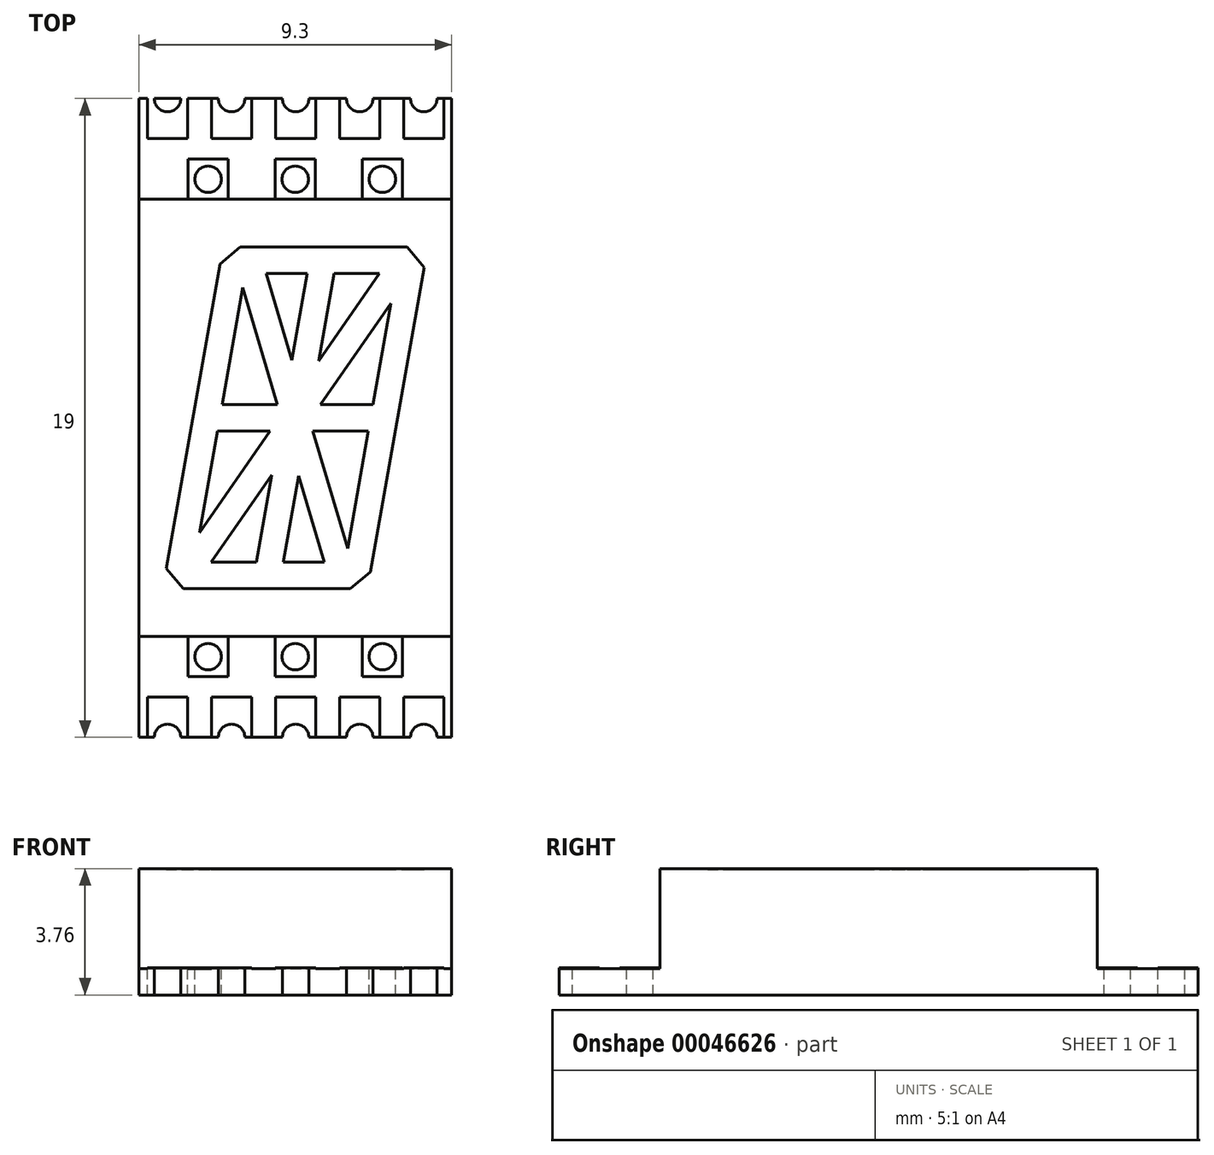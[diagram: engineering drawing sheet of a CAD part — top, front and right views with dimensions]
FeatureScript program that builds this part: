
annotation { "Feature Type Name" : "Feature", "Feature Type Description" : "" }
export const myFeature = defineFeature(function(context is Context, id is Id, definition is map)
    precondition{}
    {
        {
            var Q0;
            Q0=qCreatedBy(makeId("Top.planeOp"),FACE);
            var sketch = newSketch(context, id + "F0", { "sketchPlane" : qUnion([Q0])});
            skLineSegment(sketch, "E0.bottom", {"start": v(-4.65, -9.5) * mm, "end": v(4.65, -9.5) * mm});
            skLineSegment(sketch, "E0.top", {"start": v(-4.65, 9.5) * mm, "end": v(4.65, 9.5) * mm});
            skLineSegment(sketch, "E0.left", {"start": v(-4.65, -9.5) * mm, "end": v(-4.65, 9.5) * mm});
            skLineSegment(sketch, "E0.right", {"start": v(4.65, -9.5) * mm, "end": v(4.65, 9.5) * mm});
            skSolve(sketch);
        }
        {
            var Q0;
            Q0=makeQuery(id+"F0.imprint","IMPRINT",FACE,{"disambiguationData":[TD([[makeQuery(id+"F0.imprint","IMPRINT",EDGE,{"derivedFrom":sQuery(id+"F0.wireOp",EDGE,"E0.bottom")}),1.0]])]});
            extrude(context, id + "F1", {"entities" : qUnion([Q0]), "depth" : 0.79 * mm});
        }
        {
            var Q0;
            Q0=makeQuery(id+"F1.opExtrude","CAP_FACE",FACE,{"disambiguationData":[OSD([sQuery(id+"F0.wireOp",EDGE,"E0.bottom"),sQuery(id+"F0.wireOp",EDGE,"E0.top"),sQuery(id+"F0.wireOp",EDGE,"E0.left"),sQuery(id+"F0.wireOp",EDGE,"E0.right")])],"isStart":false});
            var sketch = newSketch(context, id + "F2", { "sketchPlane" : qUnion([Q0])});
            skLineSegment(sketch, "E1.bottom", {"start": v(-4.65, -6.5) * mm, "end": v(4.65, -6.5) * mm});
            skLineSegment(sketch, "E1.top", {"start": v(-4.65, 6.5) * mm, "end": v(4.65, 6.5) * mm});
            skLineSegment(sketch, "E1.left", {"start": v(-4.65, -6.5) * mm, "end": v(-4.65, 6.5) * mm});
            skLineSegment(sketch, "E1.right", {"start": v(4.65, -6.5) * mm, "end": v(4.65, 6.5) * mm});
            skSolve(sketch);
        }
        {
            var Q0;
            Q0=makeQuery(id+"F2.imprint","IMPRINT",FACE,{"disambiguationData":[TD([[makeQuery(id+"F2.imprint","IMPRINT",EDGE,{"derivedFrom":sQuery(id+"F2.wireOp",EDGE,"E1.bottom")}),1.0]])]});
            extrude(context, id + "F3", {"entities" : qUnion([Q0]), "operationType" : NewBodyOperationType.ADD, "depth" : 2.97 * mm});
        }
        {
            var Q0;
            {var subQ0=sQuery(id+"F0.wireOp",EDGE,"E0.bottom");var subQ1=sQuery(id+"F0.wireOp",EDGE,"E0.left");var subQ2=sQuery(id+"F0.wireOp",EDGE,"E0.right");Q0=makeQuery(id+"F3.boolean.opBoolean","SPLIT",FACE,{"disambiguationData":[TD([makeQuery(id+"F1.opExtrude","SWEPT_FACE",FACE,{"disambiguationData":[OSD([subQ0])]})])],"derivedFrom":makeQuery(id+"F1.opExtrude","CAP_FACE",FACE,{"disambiguationData":[OSD([subQ0,sQuery(id+"F0.wireOp",EDGE,"E0.top"),subQ1,subQ2])],"isStart":false})});}
            var sketch = newSketch(context, id + "F4", { "sketchPlane" : qUnion([Q0])});
            skLineSegment(sketch, "E2", {"start": v(-4.4, -9.5) * mm, "end": v(-4.4, -8.3) * mm});
            skLineSegment(sketch, "E3", {"start": v(-4.4, -8.3) * mm, "end": v(-3.2, -8.3) * mm});
            skLineSegment(sketch, "E4", {"start": v(-3.2, -8.3) * mm, "end": v(-3.2, -9.5) * mm});
            skArc(sketch, "E5", {"start": v(-3.4, -9.5) * mm, "mid": v(-3.8, -9.1) * mm, "end": v(-4.2, -9.5) * mm});
            skLineSegment(sketch, "E6", {"start": v(-4.4, -9.5) * mm, "end": v(-4.2, -9.5) * mm});
            skLineSegment(sketch, "E7", {"start": v(-3.4, -9.5) * mm, "end": v(-3.2, -9.5) * mm});
            skLineSegment(sketch, "E8", {"start": v(-4.2, -9.5) * mm, "end": v(-3.4, -9.5) * mm});
            skLineSegment(sketch, "E9.1.0.0", {"start": v(-2.49, -8.3) * mm, "end": v(-1.3, -8.3) * mm});
            skLineSegment(sketch, "E9.1.0.1", {"start": v(-2.49, -9.5) * mm, "end": v(-2.49, -8.3) * mm});
            skLineSegment(sketch, "E9.1.0.2", {"start": v(-1.3, -8.3) * mm, "end": v(-1.3, -9.5) * mm});
            skArc(sketch, "E9.1.0.3", {"start": v(-1.5, -9.5) * mm, "mid": v(-1.9, -9.1) * mm, "end": v(-2.29, -9.5) * mm});
            skLineSegment(sketch, "E9.1.0.4", {"start": v(-2.29, -9.5) * mm, "end": v(-1.5, -9.5) * mm});
            skLineSegment(sketch, "E9.1.0.5", {"start": v(-2.49, -9.5) * mm, "end": v(-2.29, -9.5) * mm});
            skLineSegment(sketch, "E9.1.0.6", {"start": v(-1.5, -9.5) * mm, "end": v(-1.3, -9.5) * mm});
            skLineSegment(sketch, "E9.2.0.0", {"start": v(-0.58, -8.3) * mm, "end": v(0.6, -8.3) * mm});
            skLineSegment(sketch, "E9.2.0.1", {"start": v(-0.58, -9.5) * mm, "end": v(-0.58, -8.3) * mm});
            skLineSegment(sketch, "E9.2.0.2", {"start": v(0.6, -8.3) * mm, "end": v(0.6, -9.5) * mm});
            skArc(sketch, "E9.2.0.3", {"start": v(0.4, -9.5) * mm, "mid": v(0.01, -9.1) * mm, "end": v(-0.38, -9.5) * mm});
            skLineSegment(sketch, "E9.2.0.4", {"start": v(-0.38, -9.5) * mm, "end": v(0.4, -9.5) * mm});
            skLineSegment(sketch, "E9.2.0.5", {"start": v(-0.58, -9.5) * mm, "end": v(-0.38, -9.5) * mm});
            skLineSegment(sketch, "E9.2.0.6", {"start": v(0.4, -9.5) * mm, "end": v(0.6, -9.5) * mm});
            skLineSegment(sketch, "E9.3.0.0", {"start": v(1.32, -8.3) * mm, "end": v(2.51, -8.3) * mm});
            skLineSegment(sketch, "E9.3.0.1", {"start": v(1.32, -9.5) * mm, "end": v(1.32, -8.3) * mm});
            skLineSegment(sketch, "E9.3.0.2", {"start": v(2.51, -8.3) * mm, "end": v(2.51, -9.5) * mm});
            skArc(sketch, "E9.3.0.3", {"start": v(2.31, -9.5) * mm, "mid": v(1.92, -9.1) * mm, "end": v(1.52, -9.5) * mm});
            skLineSegment(sketch, "E9.3.0.4", {"start": v(1.52, -9.5) * mm, "end": v(2.31, -9.5) * mm});
            skLineSegment(sketch, "E9.3.0.5", {"start": v(1.32, -9.5) * mm, "end": v(1.52, -9.5) * mm});
            skLineSegment(sketch, "E9.3.0.6", {"start": v(2.31, -9.5) * mm, "end": v(2.51, -9.5) * mm});
            skLineSegment(sketch, "E9.4.0.0", {"start": v(3.23, -8.3) * mm, "end": v(4.42, -8.3) * mm});
            skLineSegment(sketch, "E9.4.0.1", {"start": v(3.23, -9.5) * mm, "end": v(3.23, -8.3) * mm});
            skLineSegment(sketch, "E9.4.0.2", {"start": v(4.42, -8.3) * mm, "end": v(4.42, -9.5) * mm});
            skArc(sketch, "E9.4.0.3", {"start": v(4.22, -9.5) * mm, "mid": v(3.82, -9.1) * mm, "end": v(3.43, -9.5) * mm});
            skLineSegment(sketch, "E9.4.0.4", {"start": v(3.43, -9.5) * mm, "end": v(4.22, -9.5) * mm});
            skLineSegment(sketch, "E9.4.0.5", {"start": v(3.23, -9.5) * mm, "end": v(3.43, -9.5) * mm});
            skLineSegment(sketch, "E9.4.0.6", {"start": v(4.22, -9.5) * mm, "end": v(4.42, -9.5) * mm});
            skLineSegment(sketch, "E9.direction1", {"start": v(-4.4, -8.3) * mm, "end": v(-2.49, -8.3) * mm, "construction": true});
            skLineSegment(sketch, "E10", {"start": v(-9.42, 0) * mm, "end": v(7.06, 0) * mm, "construction": true});
            skLineSegment(sketch, "E11.MirrorCS", {"start": v(-1.5, 9.5) * mm, "end": v(-1.3, 9.5) * mm});
            skLineSegment(sketch, "E12.MirrorCS", {"start": v(-2.49, 9.5) * mm, "end": v(-2.29, 9.5) * mm});
            skLineSegment(sketch, "E13.MirrorCS", {"start": v(-2.29, 9.5) * mm, "end": v(-1.5, 9.5) * mm});
            skArc(sketch, "E14.MirrorCS", {"start": v(-1.5, 9.5) * mm, "mid": v(-1.9, 9.1) * mm, "end": v(-2.29, 9.5) * mm});
            skLineSegment(sketch, "E15.MirrorCS", {"start": v(-0.58, 9.5) * mm, "end": v(-0.38, 9.5) * mm});
            skArc(sketch, "E16.MirrorCS", {"start": v(-3.4, 9.5) * mm, "mid": v(-3.8, 9.1) * mm, "end": v(-4.2, 9.5) * mm});
            skLineSegment(sketch, "E17.MirrorCS", {"start": v(-3.4, 9.5) * mm, "end": v(-3.2, 9.5) * mm});
            skLineSegment(sketch, "E18.MirrorCS", {"start": v(-4.2, 9.5) * mm, "end": v(-3.4, 9.5) * mm});
            skLineSegment(sketch, "E19.MirrorCS", {"start": v(-0.38, 9.5) * mm, "end": v(0.4, 9.5) * mm});
            skLineSegment(sketch, "E20.MirrorCS", {"start": v(1.32, 9.5) * mm, "end": v(1.52, 9.5) * mm});
            skLineSegment(sketch, "E21.MirrorCS", {"start": v(1.52, 9.5) * mm, "end": v(2.31, 9.5) * mm});
            skArc(sketch, "E22.MirrorCS", {"start": v(0.4, 9.5) * mm, "mid": v(0.01, 9.1) * mm, "end": v(-0.38, 9.5) * mm});
            skLineSegment(sketch, "E23.MirrorCS", {"start": v(3.23, 9.5) * mm, "end": v(3.43, 9.5) * mm});
            skLineSegment(sketch, "E24.MirrorCS", {"start": v(2.31, 9.5) * mm, "end": v(2.51, 9.5) * mm});
            skLineSegment(sketch, "E25.MirrorCS", {"start": v(0.4, 9.5) * mm, "end": v(0.6, 9.5) * mm});
            skArc(sketch, "E26.MirrorCS", {"start": v(2.31, 9.5) * mm, "mid": v(1.92, 9.1) * mm, "end": v(1.52, 9.5) * mm});
            skLineSegment(sketch, "E27.MirrorCS", {"start": v(-4.4, 9.5) * mm, "end": v(-4.2, 9.5) * mm});
            skLineSegment(sketch, "E28.MirrorCS", {"start": v(4.22, 9.5) * mm, "end": v(4.42, 9.5) * mm});
            skLineSegment(sketch, "E29.MirrorCS", {"start": v(3.43, 9.5) * mm, "end": v(4.22, 9.5) * mm});
            skArc(sketch, "E30.MirrorCS", {"start": v(4.22, 9.5) * mm, "mid": v(3.82, 9.1) * mm, "end": v(3.43, 9.5) * mm});
            skLineSegment(sketch, "E31.MirrorCS", {"start": v(-4.4, 8.3) * mm, "end": v(-2.49, 8.3) * mm});
            skLineSegment(sketch, "E32.MirrorCS", {"start": v(-2.49, 9.5) * mm, "end": v(-2.49, 8.3) * mm});
            skLineSegment(sketch, "E33.MirrorCS", {"start": v(-1.3, 8.3) * mm, "end": v(-1.3, 9.5) * mm});
            skLineSegment(sketch, "E34.MirrorCS", {"start": v(-3.2, 8.3) * mm, "end": v(-3.2, 9.5) * mm});
            skLineSegment(sketch, "E35.MirrorCS", {"start": v(-4.4, 8.3) * mm, "end": v(-3.2, 8.3) * mm});
            skLineSegment(sketch, "E36.MirrorCS", {"start": v(-4.4, 9.5) * mm, "end": v(-4.4, 8.3) * mm});
            skLineSegment(sketch, "E37.MirrorCS", {"start": v(2.51, 8.3) * mm, "end": v(2.51, 9.5) * mm});
            skLineSegment(sketch, "E38.MirrorCS", {"start": v(1.32, 9.5) * mm, "end": v(1.32, 8.3) * mm});
            skLineSegment(sketch, "E39.MirrorCS", {"start": v(1.32, 8.3) * mm, "end": v(2.51, 8.3) * mm});
            skLineSegment(sketch, "E40.MirrorCS", {"start": v(4.42, 8.3) * mm, "end": v(4.42, 9.5) * mm});
            skLineSegment(sketch, "E41.MirrorCS", {"start": v(-2.49, 8.3) * mm, "end": v(-1.3, 8.3) * mm});
            skLineSegment(sketch, "E42.MirrorCS", {"start": v(0.6, 8.3) * mm, "end": v(0.6, 9.5) * mm});
            skLineSegment(sketch, "E43.MirrorCS", {"start": v(3.23, 9.5) * mm, "end": v(3.23, 8.3) * mm});
            skLineSegment(sketch, "E44.MirrorCS", {"start": v(3.23, 8.3) * mm, "end": v(4.42, 8.3) * mm});
            skLineSegment(sketch, "E45.MirrorCS", {"start": v(-0.58, 8.3) * mm, "end": v(0.6, 8.3) * mm});
            skLineSegment(sketch, "E46.MirrorCS", {"start": v(-0.58, 9.5) * mm, "end": v(-0.58, 8.3) * mm});
            skLineSegment(sketch, "E47.bottom", {"start": v(-3.19, -6.5) * mm, "end": v(-2, -6.5) * mm});
            skLineSegment(sketch, "E47.top", {"start": v(-3.19, -7.7) * mm, "end": v(-2, -7.7) * mm});
            skLineSegment(sketch, "E47.left", {"start": v(-3.19, -6.5) * mm, "end": v(-3.19, -7.7) * mm});
            skLineSegment(sketch, "E47.right", {"start": v(-2, -6.5) * mm, "end": v(-2, -7.7) * mm});
            skCircle(sketch, "E48", {"center": v(-2.6, -7.1) * mm, "radius": 0.4 * mm});
            skLineSegment(sketch, "E49", {"start": v(-3.19, -6.5) * mm, "end": v(-2, -7.7) * mm, "construction": true});
            skLineSegment(sketch, "E50.1.0.0", {"start": v(-0.6, -6.5) * mm, "end": v(-0.6, -7.7) * mm});
            skLineSegment(sketch, "E50.1.0.1", {"start": v(-0.6, -6.5) * mm, "end": v(0.6, -7.7) * mm, "construction": true});
            skLineSegment(sketch, "E50.1.0.2", {"start": v(-0.6, -6.5) * mm, "end": v(0.6, -6.5) * mm});
            skLineSegment(sketch, "E50.1.0.3", {"start": v(-0.6, -7.7) * mm, "end": v(0.6, -7.7) * mm});
            skCircle(sketch, "E50.1.0.4", {"center": v(0, -7.1) * mm, "radius": 0.4 * mm});
            skLineSegment(sketch, "E50.1.0.5", {"start": v(0.6, -6.5) * mm, "end": v(0.6, -7.7) * mm});
            skLineSegment(sketch, "E50.2.0.0", {"start": v(2, -6.5) * mm, "end": v(2, -7.7) * mm});
            skLineSegment(sketch, "E50.2.0.1", {"start": v(2, -6.5) * mm, "end": v(3.19, -7.7) * mm, "construction": true});
            skLineSegment(sketch, "E50.2.0.2", {"start": v(2, -6.5) * mm, "end": v(3.19, -6.5) * mm});
            skLineSegment(sketch, "E50.2.0.3", {"start": v(2, -7.7) * mm, "end": v(3.19, -7.7) * mm});
            skCircle(sketch, "E50.2.0.4", {"center": v(2.6, -7.1) * mm, "radius": 0.4 * mm});
            skLineSegment(sketch, "E50.2.0.5", {"start": v(3.19, -6.5) * mm, "end": v(3.19, -7.7) * mm});
            skLineSegment(sketch, "E50.direction1", {"start": v(-3.19, -7.7) * mm, "end": v(-0.6, -7.7) * mm, "construction": true});
            skLineSegment(sketch, "E51.MirrorCS", {"start": v(-3.19, 6.5) * mm, "end": v(-2, 7.7) * mm});
            skLineSegment(sketch, "E52.MirrorCS", {"start": v(2, 6.5) * mm, "end": v(3.19, 7.7) * mm});
            skLineSegment(sketch, "E53.MirrorCS", {"start": v(-0.6, 6.5) * mm, "end": v(-0.6, 7.7) * mm});
            skLineSegment(sketch, "E54.MirrorCS", {"start": v(-0.6, 6.5) * mm, "end": v(0.6, 7.7) * mm});
            skLineSegment(sketch, "E55.MirrorCS", {"start": v(-3.19, 6.5) * mm, "end": v(-3.19, 7.7) * mm});
            skLineSegment(sketch, "E56.MirrorCS", {"start": v(-2, 6.5) * mm, "end": v(-2, 7.7) * mm});
            skCircle(sketch, "E57.MirrorC", {"center": v(0, 7.1) * mm, "radius": 0.4 * mm});
            skLineSegment(sketch, "E58.MirrorCS", {"start": v(-3.19, 6.5) * mm, "end": v(-2, 6.5) * mm});
            skLineSegment(sketch, "E59.MirrorCS", {"start": v(-0.6, 6.5) * mm, "end": v(0.6, 6.5) * mm});
            skLineSegment(sketch, "E60.MirrorCS", {"start": v(2, 6.5) * mm, "end": v(2, 7.7) * mm});
            skLineSegment(sketch, "E61.MirrorCS", {"start": v(2, 6.5) * mm, "end": v(3.19, 6.5) * mm});
            skLineSegment(sketch, "E62.MirrorCS", {"start": v(2, 7.7) * mm, "end": v(3.19, 7.7) * mm});
            skCircle(sketch, "E63.MirrorC", {"center": v(2.6, 7.1) * mm, "radius": 0.4 * mm});
            skLineSegment(sketch, "E64.MirrorCS", {"start": v(-3.19, 7.7) * mm, "end": v(-0.6, 7.7) * mm});
            skLineSegment(sketch, "E65.MirrorCS", {"start": v(-0.6, 7.7) * mm, "end": v(0.6, 7.7) * mm});
            skLineSegment(sketch, "E66.MirrorCS", {"start": v(0.6, 6.5) * mm, "end": v(0.6, 7.7) * mm});
            skCircle(sketch, "E67.MirrorC", {"center": v(-2.6, 7.1) * mm, "radius": 0.4 * mm});
            skLineSegment(sketch, "E68.MirrorCS", {"start": v(-3.19, 7.7) * mm, "end": v(-2, 7.7) * mm});
            skLineSegment(sketch, "E69.MirrorCS", {"start": v(3.19, 6.5) * mm, "end": v(3.19, 7.7) * mm});
            skSolve(sketch);
        }
        {
            var Q0;
            Q0=makeQuery(id+"F4.imprint","IMPRINT",FACE,{"disambiguationData":[TD([[makeQuery(id+"F4.imprint","IMPRINT",EDGE,{"derivedFrom":sQuery(id+"F4.wireOp",EDGE,"E5")}),1.0]])]});
            var Q1;
            Q1=makeQuery(id+"F4.imprint","IMPRINT",FACE,{"disambiguationData":[TD([[makeQuery(id+"F4.imprint","IMPRINT",EDGE,{"derivedFrom":sQuery(id+"F4.wireOp",EDGE,"E9.1.0.3")}),1.0]])]});
            var Q2;
            Q2=makeQuery(id+"F4.imprint","IMPRINT",FACE,{"disambiguationData":[TD([[makeQuery(id+"F4.imprint","IMPRINT",EDGE,{"derivedFrom":sQuery(id+"F4.wireOp",EDGE,"E9.2.0.3")}),1.0]])]});
            var Q3;
            Q3=makeQuery(id+"F4.imprint","IMPRINT",FACE,{"disambiguationData":[TD([[makeQuery(id+"F4.imprint","IMPRINT",EDGE,{"derivedFrom":sQuery(id+"F4.wireOp",EDGE,"E9.3.0.3")}),1.0]])]});
            var Q4;
            Q4=makeQuery(id+"F4.imprint","IMPRINT",FACE,{"disambiguationData":[TD([[makeQuery(id+"F4.imprint","IMPRINT",EDGE,{"derivedFrom":sQuery(id+"F4.wireOp",EDGE,"E9.4.0.3")}),1.0]])]});
            var Q5;
            Q5=makeQuery(id+"F4.imprint","IMPRINT",FACE,{"disambiguationData":[TD([[makeQuery(id+"F4.imprint","IMPRINT",EDGE,{"derivedFrom":sQuery(id+"F4.wireOp",EDGE,"E50.2.0.4")}),1.0]])]});
            var Q6;
            Q6=makeQuery(id+"F4.imprint","IMPRINT",FACE,{"disambiguationData":[TD([[makeQuery(id+"F4.imprint","IMPRINT",EDGE,{"derivedFrom":sQuery(id+"F4.wireOp",EDGE,"E50.1.0.4")}),1.0]])]});
            var Q7;
            Q7=makeQuery(id+"F4.imprint","IMPRINT",FACE,{"disambiguationData":[TD([[makeQuery(id+"F4.imprint","IMPRINT",EDGE,{"derivedFrom":sQuery(id+"F4.wireOp",EDGE,"E48")}),1.0]])]});
            var Q8;
            {var subQ0=sQuery(id+"F4.wireOp",EDGE,"E67.MirrorC");var subQ1=sQuery(id+"F4.wireOp",EDGE,"E51.MirrorCS");var subQ3=makeQuery(id+"F4.imprint","INTERSECT",VERTEX,{"disambiguationData":[OD(0.0)],"derivedFrom":[subQ1,subQ0]});Q8=makeQuery(id+"F4.imprint","IMPRINT",FACE,{"disambiguationData":[TD([[makeQuery(id+"F4.imprint","IMPRINT",EDGE,{"disambiguationData":[TD([[subQ3,-1.0]])],"derivedFrom":subQ1}),1.0]])]});}
            var Q9;
            {var subQ0=sQuery(id+"F4.wireOp",EDGE,"E67.MirrorC");var subQ1=sQuery(id+"F4.wireOp",EDGE,"E51.MirrorCS");var subQ3=makeQuery(id+"F4.imprint","INTERSECT",VERTEX,{"disambiguationData":[OD(0.0)],"derivedFrom":[subQ1,subQ0]});Q9=makeQuery(id+"F4.imprint","IMPRINT",FACE,{"disambiguationData":[TD([[makeQuery(id+"F4.imprint","IMPRINT",EDGE,{"disambiguationData":[TD([[subQ3,-1.0]])],"derivedFrom":subQ1}),-1.0]])]});}
            var Q10;
            {var subQ0=sQuery(id+"F4.wireOp",EDGE,"E57.MirrorC");var subQ1=sQuery(id+"F4.wireOp",EDGE,"E54.MirrorCS");var subQ3=makeQuery(id+"F4.imprint","INTERSECT",VERTEX,{"disambiguationData":[OD(0.0)],"derivedFrom":[subQ1,subQ0]});Q10=makeQuery(id+"F4.imprint","IMPRINT",FACE,{"disambiguationData":[TD([[makeQuery(id+"F4.imprint","IMPRINT",EDGE,{"disambiguationData":[TD([[subQ3,-1.0]])],"derivedFrom":subQ1}),1.0]])]});}
            var Q11;
            {var subQ0=sQuery(id+"F4.wireOp",EDGE,"E57.MirrorC");var subQ1=sQuery(id+"F4.wireOp",EDGE,"E54.MirrorCS");var subQ3=makeQuery(id+"F4.imprint","INTERSECT",VERTEX,{"disambiguationData":[OD(0.0)],"derivedFrom":[subQ1,subQ0]});Q11=makeQuery(id+"F4.imprint","IMPRINT",FACE,{"disambiguationData":[TD([[makeQuery(id+"F4.imprint","IMPRINT",EDGE,{"disambiguationData":[TD([[subQ3,-1.0]])],"derivedFrom":subQ1}),-1.0]])]});}
            var Q12;
            {var subQ0=sQuery(id+"F4.wireOp",EDGE,"E63.MirrorC");var subQ1=sQuery(id+"F4.wireOp",EDGE,"E52.MirrorCS");var subQ3=makeQuery(id+"F4.imprint","INTERSECT",VERTEX,{"disambiguationData":[OD(0.0)],"derivedFrom":[subQ1,subQ0]});Q12=makeQuery(id+"F4.imprint","IMPRINT",FACE,{"disambiguationData":[TD([[makeQuery(id+"F4.imprint","IMPRINT",EDGE,{"disambiguationData":[TD([[subQ3,-1.0]])],"derivedFrom":subQ1}),1.0]])]});}
            var Q13;
            {var subQ0=sQuery(id+"F4.wireOp",EDGE,"E63.MirrorC");var subQ1=sQuery(id+"F4.wireOp",EDGE,"E52.MirrorCS");var subQ3=makeQuery(id+"F4.imprint","INTERSECT",VERTEX,{"disambiguationData":[OD(0.0)],"derivedFrom":[subQ1,subQ0]});Q13=makeQuery(id+"F4.imprint","IMPRINT",FACE,{"disambiguationData":[TD([[makeQuery(id+"F4.imprint","IMPRINT",EDGE,{"disambiguationData":[TD([[subQ3,-1.0]])],"derivedFrom":subQ1}),-1.0]])]});}
            var Q14;
            Q14=makeQuery(id+"F4.imprint","IMPRINT",FACE,{"disambiguationData":[TD([[makeQuery(id+"F4.imprint","IMPRINT",EDGE,{"derivedFrom":sQuery(id+"F4.wireOp",EDGE,"E16.MirrorCS")}),-1.0]])]});
            var Q15;
            Q15=makeQuery(id+"F4.imprint","IMPRINT",FACE,{"disambiguationData":[TD([[makeQuery(id+"F4.imprint","IMPRINT",EDGE,{"derivedFrom":sQuery(id+"F4.wireOp",EDGE,"E13.MirrorCS")}),-1.0]])]});
            var Q16;
            Q16=makeQuery(id+"F4.imprint","IMPRINT",FACE,{"disambiguationData":[TD([[makeQuery(id+"F4.imprint","IMPRINT",EDGE,{"derivedFrom":sQuery(id+"F4.wireOp",EDGE,"E19.MirrorCS")}),-1.0]])]});
            var Q17;
            Q17=makeQuery(id+"F4.imprint","IMPRINT",FACE,{"disambiguationData":[TD([[makeQuery(id+"F4.imprint","IMPRINT",EDGE,{"derivedFrom":sQuery(id+"F4.wireOp",EDGE,"E21.MirrorCS")}),-1.0]])]});
            var Q18;
            Q18=makeQuery(id+"F4.imprint","IMPRINT",FACE,{"disambiguationData":[TD([[makeQuery(id+"F4.imprint","IMPRINT",EDGE,{"derivedFrom":sQuery(id+"F4.wireOp",EDGE,"E29.MirrorCS")}),-1.0]])]});
            extrude(context, id + "F5", {"entities" : qUnion([Q0, Q1, Q2, Q3, Q4, Q5, Q6, Q7, Q8, Q9, Q10, Q11, Q12, Q13, Q14, Q15, Q16, Q17, Q18]), "operationType" : NewBodyOperationType.REMOVE, "oppositeDirection" : true, "depth" : 25.4 * mm});
        }
        {
            var Q0;
            Q0=makeQuery(id+"F4.imprint","IMPRINT",FACE,{"disambiguationData":[TD([[makeQuery(id+"F4.imprint","IMPRINT",EDGE,{"derivedFrom":sQuery(id+"F4.wireOp",EDGE,"E16.MirrorCS")}),1.0]])]});
            var Q1;
            Q1=makeQuery(id+"F4.imprint","IMPRINT",FACE,{"disambiguationData":[TD([[makeQuery(id+"F4.imprint","IMPRINT",EDGE,{"derivedFrom":sQuery(id+"F4.wireOp",EDGE,"E11.MirrorCS")}),-1.0]])]});
            var Q2;
            Q2=makeQuery(id+"F4.imprint","IMPRINT",FACE,{"disambiguationData":[TD([[makeQuery(id+"F4.imprint","IMPRINT",EDGE,{"derivedFrom":sQuery(id+"F4.wireOp",EDGE,"E15.MirrorCS")}),-1.0]])]});
            var Q3;
            Q3=makeQuery(id+"F4.imprint","IMPRINT",FACE,{"disambiguationData":[TD([[makeQuery(id+"F4.imprint","IMPRINT",EDGE,{"derivedFrom":sQuery(id+"F4.wireOp",EDGE,"E20.MirrorCS")}),-1.0]])]});
            var Q4;
            Q4=makeQuery(id+"F4.imprint","IMPRINT",FACE,{"disambiguationData":[TD([[makeQuery(id+"F4.imprint","IMPRINT",EDGE,{"derivedFrom":sQuery(id+"F4.wireOp",EDGE,"E23.MirrorCS")}),-1.0]])]});
            var Q5;
            Q5=makeQuery(id+"F4.imprint","IMPRINT",FACE,{"disambiguationData":[TD([[makeQuery(id+"F4.imprint","IMPRINT",EDGE,{"derivedFrom":sQuery(id+"F4.wireOp",EDGE,"E9.1.0.0")}),-1.0]])]});
            var Q6;
            Q6=makeQuery(id+"F4.imprint","IMPRINT",FACE,{"disambiguationData":[TD([[makeQuery(id+"F4.imprint","IMPRINT",EDGE,{"derivedFrom":sQuery(id+"F4.wireOp",EDGE,"E2")}),-1.0]])]});
            var Q7;
            Q7=makeQuery(id+"F4.imprint","IMPRINT",FACE,{"disambiguationData":[TD([[makeQuery(id+"F4.imprint","IMPRINT",EDGE,{"derivedFrom":sQuery(id+"F4.wireOp",EDGE,"E9.2.0.0")}),-1.0]])]});
            var Q8;
            Q8=makeQuery(id+"F4.imprint","IMPRINT",FACE,{"disambiguationData":[TD([[makeQuery(id+"F4.imprint","IMPRINT",EDGE,{"derivedFrom":sQuery(id+"F4.wireOp",EDGE,"E9.3.0.0")}),-1.0]])]});
            var Q9;
            Q9=makeQuery(id+"F4.imprint","IMPRINT",FACE,{"disambiguationData":[TD([[makeQuery(id+"F4.imprint","IMPRINT",EDGE,{"derivedFrom":sQuery(id+"F4.wireOp",EDGE,"E9.4.0.0")}),-1.0]])]});
            var Q10;
            Q10=makeQuery(id+"F4.imprint","IMPRINT",FACE,{"disambiguationData":[TD([[makeQuery(id+"F4.imprint","IMPRINT",EDGE,{"derivedFrom":sQuery(id+"F4.wireOp",EDGE,"E50.2.0.0")}),1.0]])]});
            var Q11;
            Q11=makeQuery(id+"F4.imprint","IMPRINT",FACE,{"disambiguationData":[TD([[makeQuery(id+"F4.imprint","IMPRINT",EDGE,{"derivedFrom":sQuery(id+"F4.wireOp",EDGE,"E50.1.0.0")}),1.0]])]});
            var Q12;
            Q12=makeQuery(id+"F4.imprint","IMPRINT",FACE,{"disambiguationData":[TD([[makeQuery(id+"F4.imprint","IMPRINT",EDGE,{"derivedFrom":sQuery(id+"F4.wireOp",EDGE,"E47.bottom")}),-1.0]])]});
            var Q13;
            {var subQ5=sQuery(id+"F4.wireOp",EDGE,"E56.MirrorCS");Q13=makeQuery(id+"F4.imprint","IMPRINT",FACE,{"disambiguationData":[TD([[makeQuery(id+"F4.imprint","IMPRINT",EDGE,{"derivedFrom":subQ5}),1.0]])]});}
            var Q14;
            {var subQ4=sQuery(id+"F4.wireOp",EDGE,"E53.MirrorCS");Q14=makeQuery(id+"F4.imprint","IMPRINT",FACE,{"disambiguationData":[TD([[makeQuery(id+"F4.imprint","IMPRINT",EDGE,{"derivedFrom":subQ4}),-1.0]])]});}
            var Q15;
            {var subQ4=sQuery(id+"F4.wireOp",EDGE,"E59.MirrorCS");Q15=makeQuery(id+"F4.imprint","IMPRINT",FACE,{"disambiguationData":[TD([[makeQuery(id+"F4.imprint","IMPRINT",EDGE,{"derivedFrom":subQ4}),1.0]])]});}
            var Q16;
            {var subQ4=sQuery(id+"F4.wireOp",EDGE,"E61.MirrorCS");Q16=makeQuery(id+"F4.imprint","IMPRINT",FACE,{"disambiguationData":[TD([[makeQuery(id+"F4.imprint","IMPRINT",EDGE,{"derivedFrom":subQ4}),1.0]])]});}
            var Q17;
            {var subQ4=sQuery(id+"F4.wireOp",EDGE,"E55.MirrorCS");Q17=makeQuery(id+"F4.imprint","IMPRINT",FACE,{"disambiguationData":[TD([[makeQuery(id+"F4.imprint","IMPRINT",EDGE,{"derivedFrom":subQ4}),-1.0]])]});}
            var Q18;
            {var subQ3=sQuery(id+"F4.wireOp",EDGE,"E60.MirrorCS");Q18=makeQuery(id+"F4.imprint","IMPRINT",FACE,{"disambiguationData":[TD([[makeQuery(id+"F4.imprint","IMPRINT",EDGE,{"derivedFrom":subQ3}),-1.0]])]});}
            extrude(context, id + "F6", {"entities" : qUnion([Q0, Q1, Q2, Q3, Q4, Q5, Q6, Q7, Q8, Q9, Q10, Q11, Q12, Q13, Q14, Q15, Q16, Q17, Q18]), "operationType" : NewBodyOperationType.ADD, "depth" : 0.03 * mm});
        }
        {
            var Q0;
            Q0=makeQuery(id+"F3.opExtrude","CAP_FACE",FACE,{"disambiguationData":[OSD([sQuery(id+"F2.wireOp",EDGE,"E1.bottom"),sQuery(id+"F2.wireOp",EDGE,"E1.top"),sQuery(id+"F2.wireOp",EDGE,"E1.left"),sQuery(id+"F2.wireOp",EDGE,"E1.right")])],"isStart":false});
            var sketch = newSketch(context, id + "F7", { "sketchPlane" : qUnion([Q0])});
            skLineSegment(sketch, "E70", {"start": v(-2.24, 4.57) * mm, "end": v(-3.83, -4.48) * mm});
            skLineSegment(sketch, "E71", {"start": v(-3.33, -5.08) * mm, "end": v(1.63, -5.08) * mm});
            skLineSegment(sketch, "E72", {"start": v(2.24, -4.57) * mm, "end": v(3.83, 4.48) * mm});
            skLineSegment(sketch, "E73", {"start": v(3.33, 5.08) * mm, "end": v(-1.63, 5.08) * mm});
            skLineSegment(sketch, "E74.0", {"start": v(2.5, 4.3) * mm, "end": v(1.16, 4.3) * mm});
            skLineSegment(sketch, "E74.1", {"start": v(1.49, -4.3) * mm, "end": v(2.17, -0.4) * mm});
            skLineSegment(sketch, "E74.2", {"start": v(-3, -4.3) * mm, "end": v(1.49, -4.3) * mm});
            skLineSegment(sketch, "E74.3", {"start": v(-1.56, 3.88) * mm, "end": v(-2.17, 0.4) * mm});
            skLineSegment(sketch, "E75", {"start": v(0.36, 4.3) * mm, "end": v(-0.1, 1.72) * mm});
            skLineSegment(sketch, "E76", {"start": v(1.16, 4.3) * mm, "end": v(0.7, 1.7) * mm});
            skLineSegment(sketch, "E77", {"start": v(-2.17, 0.4) * mm, "end": v(-0.53, 0.4) * mm});
            skLineSegment(sketch, "E78", {"start": v(-2.31, -0.4) * mm, "end": v(-0.75, -0.4) * mm});
            skLineSegment(sketch, "E79", {"start": v(-0.15, -0.87) * mm, "end": v(-0.65, -3.68) * mm, "construction": true});
            skLineSegment(sketch, "E80", {"start": v(-1.63, 5.08) * mm, "end": v(-2.24, 4.57) * mm});
            skLineSegment(sketch, "E81", {"start": v(-2.24, 4.57) * mm, "end": v(-2.15, 5.08) * mm});
            skLineSegment(sketch, "E82", {"start": v(1.63, -5.08) * mm, "end": v(2.24, -4.57) * mm});
            skLineSegment(sketch, "E83", {"start": v(3.33, 5.08) * mm, "end": v(3.83, 4.48) * mm});
            skLineSegment(sketch, "E84", {"start": v(-3.83, -4.48) * mm, "end": v(-3.33, -5.08) * mm});
            skLineSegment(sketch, "E85.trimOffspring", {"start": v(-2.31, -0.4) * mm, "end": v(-3, -4.3) * mm});
            skLineSegment(sketch, "E86.trimOffspring", {"start": v(2.31, 0.4) * mm, "end": v(2.85, 3.41) * mm});
            skLineSegment(sketch, "E87.trimOffspring", {"start": v(0.36, 4.3) * mm, "end": v(-0.86, 4.3) * mm});
            skLineSegment(sketch, "E88.trimOffspring", {"start": v(0.75, 0.4) * mm, "end": v(2.31, 0.4) * mm});
            skLineSegment(sketch, "E89.trimOffspring", {"start": v(0.53, -0.4) * mm, "end": v(2.17, -0.4) * mm});
            skLineSegment(sketch, "E90.trimOffspring", {"start": v(-0.7, -1.7) * mm, "end": v(-1.16, -4.3) * mm});
            skLineSegment(sketch, "E91.trimOffspring", {"start": v(0.1, -1.72) * mm, "end": v(-0.36, -4.3) * mm});
            skLineSegment(sketch, "E92", {"start": v(-0.86, 4.3) * mm, "end": v(-0.1, 1.72) * mm});
            skLineSegment(sketch, "E93", {"start": v(-1.56, 3.88) * mm, "end": v(-0.53, 0.4) * mm});
            skLineSegment(sketch, "E94", {"start": v(-2.85, -3.41) * mm, "end": v(-0.75, -0.4) * mm});
            skLineSegment(sketch, "E95", {"start": v(-2.5, -4.3) * mm, "end": v(-0.7, -1.7) * mm});
            skLineSegment(sketch, "E96.trimOffspring", {"start": v(0.7, 1.7) * mm, "end": v(2.5, 4.3) * mm});
            skLineSegment(sketch, "E97.trimOffspring", {"start": v(-0.15, -0.87) * mm, "end": v(-0.14, -0.9) * mm});
            skLineSegment(sketch, "E98.trimOffspring", {"start": v(0.75, 0.4) * mm, "end": v(2.85, 3.41) * mm});
            skLineSegment(sketch, "E99.trimOffspring", {"start": v(0.53, -0.4) * mm, "end": v(1.56, -3.88) * mm});
            skLineSegment(sketch, "E100.trimOffspring", {"start": v(0.1, -1.72) * mm, "end": v(0.86, -4.3) * mm});
            skLineSegment(sketch, "E101.trimOffspring", {"start": v(-0.16, -0.93) * mm, "end": v(-0.14, -0.9) * mm});
            skPoint(sketch, "E102.orphan", {"position": v(0, 0) * mm});
            skSolve(sketch);
        }
        {
            var Q0;
            Q0=makeQuery(id+"F7.imprint","IMPRINT",FACE,{"disambiguationData":[TD([[makeQuery(id+"F7.imprint","IMPRINT",EDGE,{"derivedFrom":sQuery(id+"F7.wireOp",EDGE,"E70")}),1.0]])]});
            extrude(context, id + "F8", {"entities" : qUnion([Q0]), "operationType" : NewBodyOperationType.REMOVE, "oppositeDirection" : true, "depth" : 0.03 * mm});
        }
    });
